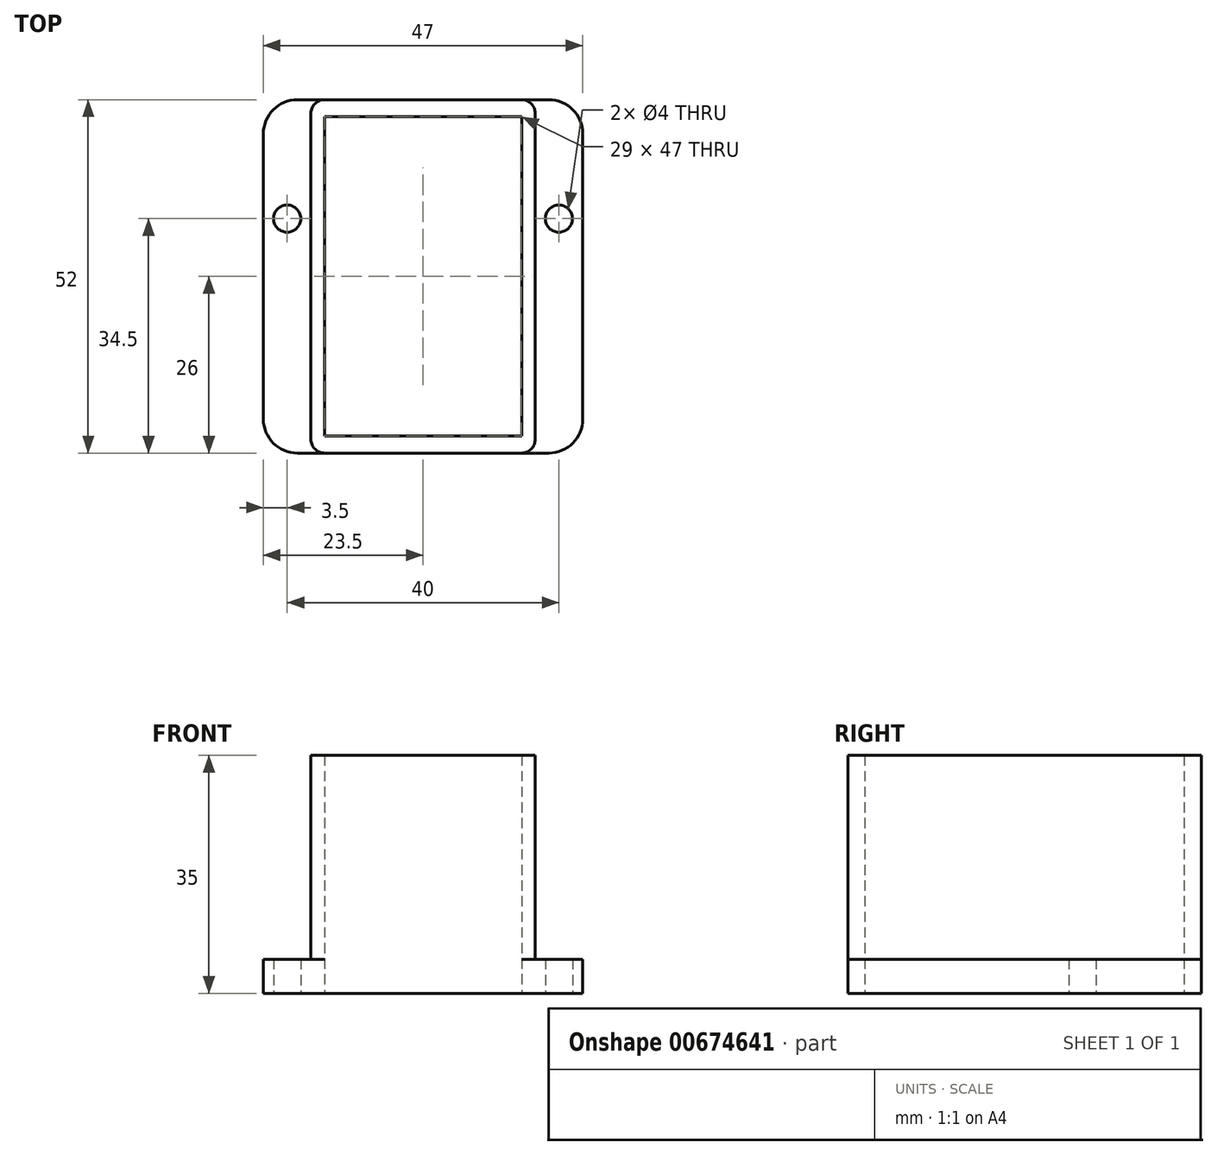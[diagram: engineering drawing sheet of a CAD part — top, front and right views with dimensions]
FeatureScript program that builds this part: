
annotation { "Feature Type Name" : "Feature", "Feature Type Description" : "" }
export const myFeature = defineFeature(function(context is Context, id is Id, definition is map)
    precondition{}
    {
        {
            var Q0;
            Q0=qCreatedBy(makeId("Top.planeOp"),FACE);
            var sketch = newSketch(context, id + "F0", { "sketchPlane" : qUnion([Q0])});
            skLineSegment(sketch, "E0.bottom", {"start": v(14.5, 23.5) * mm, "end": v(-14.5, 23.5) * mm});
            skLineSegment(sketch, "E0.top", {"start": v(14.5, -23.5) * mm, "end": v(-14.5, -23.5) * mm});
            skLineSegment(sketch, "E0.left", {"start": v(14.5, 23.5) * mm, "end": v(14.5, -23.5) * mm});
            skLineSegment(sketch, "E0.right", {"start": v(-14.5, 23.5) * mm, "end": v(-14.5, -23.5) * mm});
            skPoint(sketch, "E0.middle", {"position": v(0, 0) * mm});
            skLineSegment(sketch, "E1.bottom", {"start": v(23.5, 26) * mm, "end": v(-23.5, 26) * mm});
            skLineSegment(sketch, "E1.top", {"start": v(23.5, -26) * mm, "end": v(-23.5, -26) * mm});
            skLineSegment(sketch, "E1.left", {"start": v(23.5, 26) * mm, "end": v(23.5, -26) * mm});
            skLineSegment(sketch, "E1.right", {"start": v(-23.5, 26) * mm, "end": v(-23.5, -26) * mm});
            skLineSegment(sketch, "E2.bottom", {"start": v(16.5, 26) * mm, "end": v(-16.5, 26) * mm});
            skLineSegment(sketch, "E2.top", {"start": v(16.5, -26) * mm, "end": v(-16.5, -26) * mm});
            skLineSegment(sketch, "E2.left", {"start": v(16.5, 26) * mm, "end": v(16.5, -26) * mm});
            skLineSegment(sketch, "E2.right", {"start": v(-16.5, 26) * mm, "end": v(-16.5, -26) * mm});
            skLineSegment(sketch, "E3", {"start": v(-20, 8.5) * mm, "end": v(20, 8.5) * mm, "construction": true});
            skCircle(sketch, "E4", {"center": v(-20, 8.5) * mm, "radius": 2 * mm});
            skCircle(sketch, "E5", {"center": v(20, 8.5) * mm, "radius": 2 * mm});
            skLineSegment(sketch, "E6", {"start": v(14.5, 23.5) * mm, "end": v(14.5, 8.5) * mm, "construction": true});
            skLineSegment(sketch, "E7", {"start": v(0, 8.5) * mm, "end": v(0, 45.29) * mm, "construction": true});
            skLineSegment(sketch, "E8", {"start": v(0, 8.5) * mm, "end": v(-3.4, 0) * mm, "construction": true});
            skSolve(sketch);
        }
        {
            var Q0;
            {var subQ1=sQuery(id+"F0.wireOp",EDGE,"E1.right");Q0=makeQuery(id+"F0.imprint","IMPRINT",FACE,{"disambiguationData":[TD([[makeQuery(id+"F0.imprint","IMPRINT",EDGE,{"derivedFrom":subQ1}),1.0]])]});}
            extrude(context, id + "F1", {"entities" : qUnion([Q0]), "depth" : 5 * mm, "offsetDistance" : 25 * mm});
        }
        {
            var Q0;
            Q0=makeQuery(id+"F0.imprint","IMPRINT",FACE,{"disambiguationData":[TD([[makeQuery(id+"F0.imprint","IMPRINT",EDGE,{"derivedFrom":sQuery(id+"F0.wireOp",EDGE,"E0.bottom")}),-1.0]])]});
            extrude(context, id + "F2", {"entities" : qUnion([Q0]), "operationType" : NewBodyOperationType.ADD, "depth" : 35 * mm, "offsetDistance" : 25 * mm});
        }
        {
            var Q0;
            {var subQ1=sQuery(id+"F0.wireOp",EDGE,"E1.left");Q0=makeQuery(id+"F0.imprint","IMPRINT",FACE,{"disambiguationData":[TD([[makeQuery(id+"F0.imprint","IMPRINT",EDGE,{"derivedFrom":subQ1}),-1.0]])]});}
            extrude(context, id + "F3", {"entities" : qUnion([Q0]), "operationType" : NewBodyOperationType.ADD, "depth" : 5 * mm, "offsetDistance" : 25 * mm});
        }
        {
            var Q0;
            Q0=makeQuery(id+"F1.opExtrude","SWEPT_EDGE",EDGE,{"disambiguationData":[OSD([sQuery(id+"F0.wireOp",EDGE,"E1.top"),sQuery(id+"F0.wireOp",EDGE,"E1.right")])]});
            var Q1;
            Q1=makeQuery(id+"F3.opExtrude","SWEPT_EDGE",EDGE,{"disambiguationData":[OSD([sQuery(id+"F0.wireOp",EDGE,"E1.top"),sQuery(id+"F0.wireOp",EDGE,"E1.left")])]});
            var Q2;
            Q2=makeQuery(id+"F3.opExtrude","SWEPT_EDGE",EDGE,{"disambiguationData":[OSD([sQuery(id+"F0.wireOp",EDGE,"E1.bottom"),sQuery(id+"F0.wireOp",EDGE,"E1.left")])]});
            var Q3;
            Q3=makeQuery(id+"F1.opExtrude","SWEPT_EDGE",EDGE,{"disambiguationData":[OSD([sQuery(id+"F0.wireOp",EDGE,"E1.bottom"),sQuery(id+"F0.wireOp",EDGE,"E1.right")])]});
            fillet(context, id + "F4", {"entities" : qUnion([Q0, Q1, Q2, Q3]), "radius" : 5 * mm, "tangentPropagation" : true, "allowEdgeOverflow" : false});
        }
        {
            var Q0;
            Q0=makeQuery(id+"F2.opExtrude","SWEPT_EDGE",EDGE,{"disambiguationData":[OSD([sQuery(id+"F0.wireOp",EDGE,"E1.top"),sQuery(id+"F0.wireOp",EDGE,"E2.top"),sQuery(id+"F0.wireOp",EDGE,"E2.right")])]});
            var Q1;
            Q1=makeQuery(id+"F2.opExtrude","SWEPT_EDGE",EDGE,{"disambiguationData":[OSD([sQuery(id+"F0.wireOp",EDGE,"E1.top"),sQuery(id+"F0.wireOp",EDGE,"E2.top"),sQuery(id+"F0.wireOp",EDGE,"E2.left")])]});
            var Q2;
            Q2=makeQuery(id+"F2.opExtrude","SWEPT_EDGE",EDGE,{"disambiguationData":[OSD([sQuery(id+"F0.wireOp",EDGE,"E1.bottom"),sQuery(id+"F0.wireOp",EDGE,"E2.bottom"),sQuery(id+"F0.wireOp",EDGE,"E2.left")])]});
            var Q3;
            Q3=makeQuery(id+"F2.opExtrude","SWEPT_EDGE",EDGE,{"disambiguationData":[OSD([sQuery(id+"F0.wireOp",EDGE,"E1.bottom"),sQuery(id+"F0.wireOp",EDGE,"E2.bottom"),sQuery(id+"F0.wireOp",EDGE,"E2.right")])]});
            fillet(context, id + "F5", {"entities" : qUnion([Q0, Q1, Q2, Q3]), "radius" : 2 * mm, "tangentPropagation" : true, "allowEdgeOverflow" : false});
        }
    });
